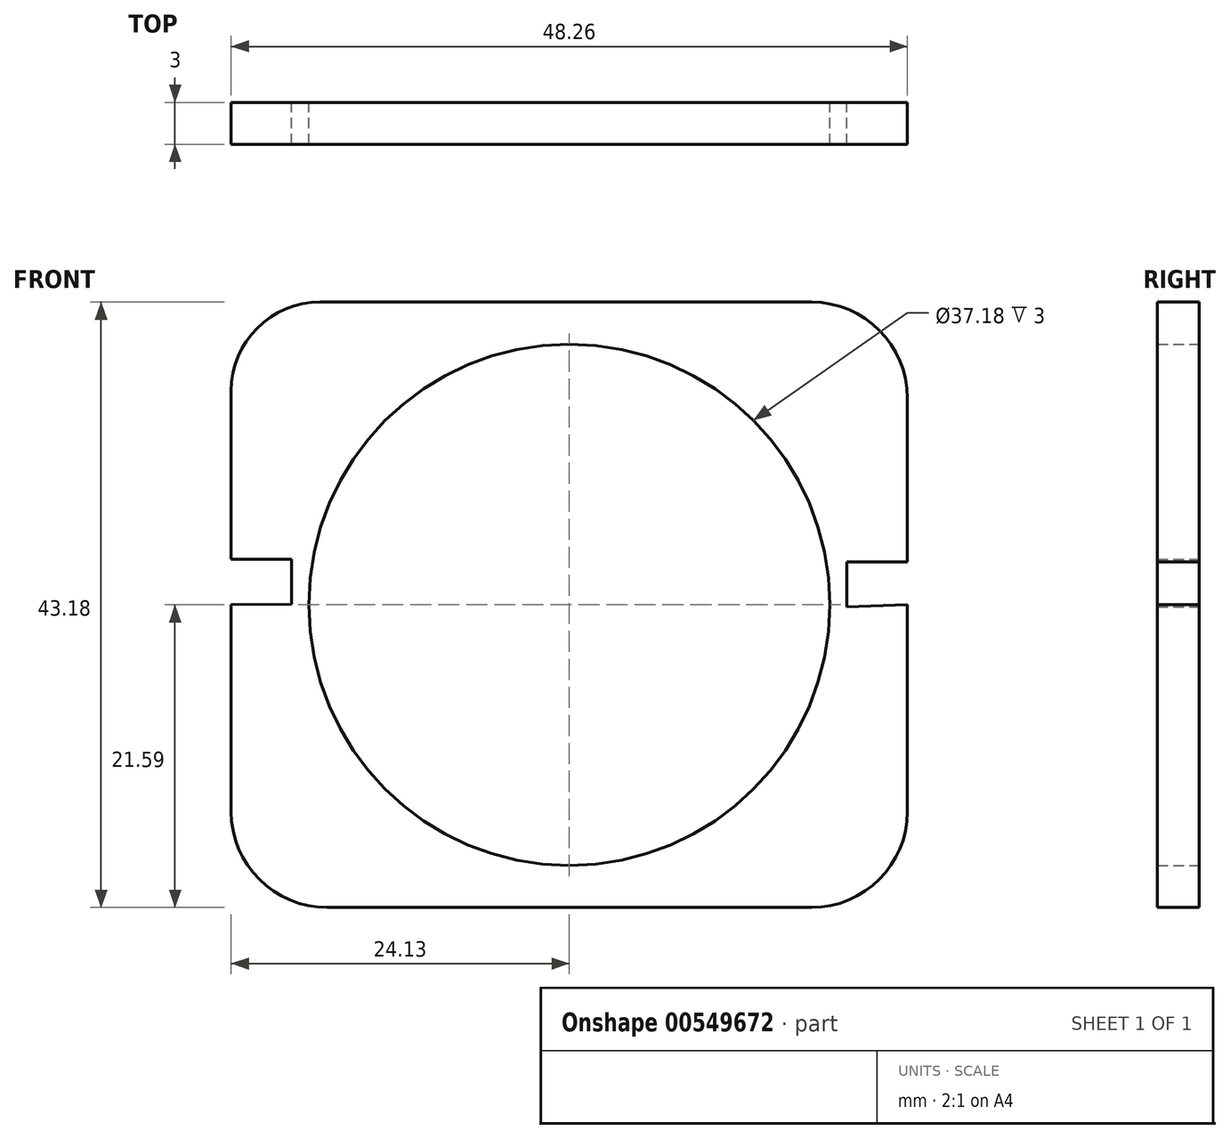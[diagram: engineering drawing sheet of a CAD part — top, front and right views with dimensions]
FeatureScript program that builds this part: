
annotation { "Feature Type Name" : "Feature", "Feature Type Description" : "" }
export const myFeature = defineFeature(function(context is Context, id is Id, definition is map)
    precondition{}
    {
        {
            var Q0;
            Q0=qCreatedBy(makeId("Front.planeOp"),FACE);
            var sketch = newSketch(context, id + "F0", { "sketchPlane" : qUnion([Q0])});
            skLineSegment(sketch, "E0.bottom", {"start": v(-17.78, 21.59) * mm, "end": v(17.28, 21.59) * mm});
            skLineSegment(sketch, "E0.top", {"start": v(-17.28, -21.59) * mm, "end": v(17.28, -21.59) * mm});
            skLineSegment(sketch, "E0.left", {"start": v(-24.13, 15.24) * mm, "end": v(-24.13, -14.74) * mm});
            skLineSegment(sketch, "E0.right", {"start": v(24.13, 14.74) * mm, "end": v(24.13, -14.74) * mm});
            skPoint(sketch, "E0.middle", {"position": v(0, 0) * mm});
            skCircle(sketch, "E1", {"center": v(0, 0) * mm, "radius": 18.59 * mm});
            skLineSegment(sketch, "E2", {"start": v(-19.81, 3.26) * mm, "end": v(-19.81, 0.06) * mm});
            skLineSegment(sketch, "E3", {"start": v(-19.81, 3.26) * mm, "end": v(-24.13, 3.26) * mm});
            skLineSegment(sketch, "E4", {"start": v(-24.13, 3.26) * mm, "end": v(-24.13, 0) * mm});
            skLineSegment(sketch, "E5", {"start": v(-24.13, 0) * mm, "end": v(-19.81, 0.06) * mm});
            skLineSegment(sketch, "E6", {"start": v(19.81, 3.06) * mm, "end": v(19.81, -0.14) * mm});
            skLineSegment(sketch, "E7", {"start": v(19.81, 3.06) * mm, "end": v(24.13, 3.06) * mm});
            skPoint(sketch, "E7.endSnap0", {"position": v(24.13, 0) * mm});
            skLineSegment(sketch, "E8", {"start": v(24.13, 3.06) * mm, "end": v(24.13, 0) * mm});
            skLineSegment(sketch, "E9", {"start": v(24.13, 0) * mm, "end": v(19.81, -0.14) * mm});
            skPoint(sketch, "E10.visualSharp", {"position": v(-24.13, 21.59) * mm});
            skArc(sketch, "E10.filletArc", {"start": v(-17.78, 21.59) * mm, "mid": v(-22.27, 19.73) * mm, "end": v(-24.13, 15.24) * mm});
            skPoint(sketch, "E11.visualSharp", {"position": v(-24.13, -21.59) * mm});
            skArc(sketch, "E11.filletArc", {"start": v(-24.13, -14.74) * mm, "mid": v(-22.12, -19.58) * mm, "end": v(-17.28, -21.59) * mm});
            skPoint(sketch, "E12.visualSharp", {"position": v(24.13, 21.59) * mm});
            skArc(sketch, "E12.filletArc", {"start": v(24.13, 14.74) * mm, "mid": v(22.12, 19.58) * mm, "end": v(17.28, 21.59) * mm});
            skPoint(sketch, "E13.visualSharp", {"position": v(24.13, -21.59) * mm});
            skArc(sketch, "E13.filletArc", {"start": v(17.28, -21.59) * mm, "mid": v(22.12, -19.58) * mm, "end": v(24.13, -14.74) * mm});
            skSolve(sketch);
        }
        {
            var Q0;
            Q0=makeQuery(id+"F0.imprint","IMPRINT",FACE,{"disambiguationData":[TD([[makeQuery(id+"F0.imprint","IMPRINT",EDGE,{"derivedFrom":sQuery(id+"F0.wireOp",EDGE,"E0.bottom")}),-1.0]])]});
            extrude(context, id + "F1", {"entities" : qUnion([Q0]), "depth" : 3 * mm, "offsetDistance" : 25.4 * mm});
        }
    });
